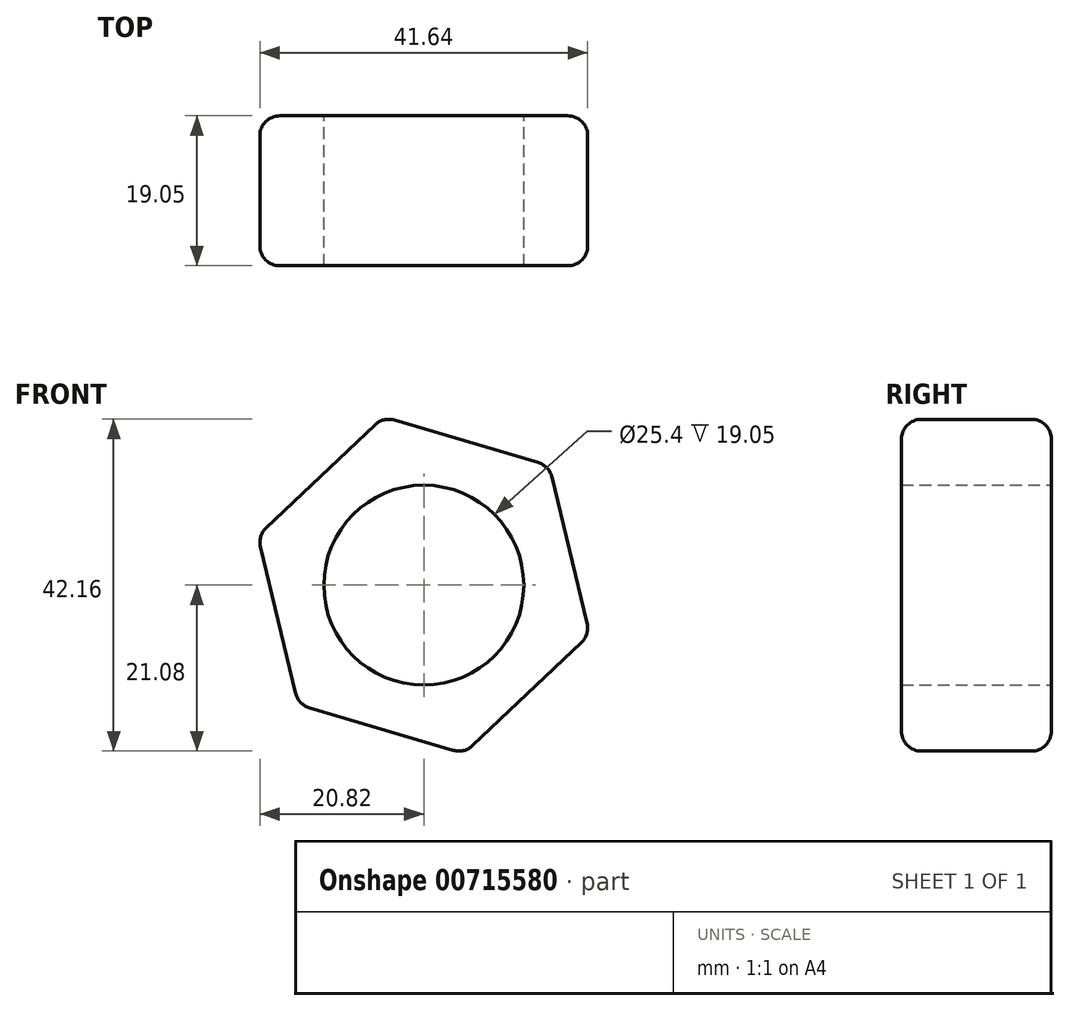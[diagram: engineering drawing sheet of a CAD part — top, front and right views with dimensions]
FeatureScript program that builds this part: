
annotation { "Feature Type Name" : "Feature", "Feature Type Description" : "" }
export const myFeature = defineFeature(function(context is Context, id is Id, definition is map)
    precondition{}
    {
        {
            var Q0;
            Q0=qCreatedBy(makeId("Front.planeOp"),FACE);
            var sketch = newSketch(context, id + "F0", { "sketchPlane" : qUnion([Q0])});
            skCircle(sketch, "E0", {"center": v(0, 0) * mm, "radius": 12.7 * mm});
            skCircle(sketch, "E1.cCircle", {"center": v(0, 0) * mm, "radius": 19.05 * mm, "construction": true});
            skLineSegment(sketch, "E1.0", {"start": v(21.1, -6.24) * mm, "end": v(5.14, -21.39) * mm});
            skLineSegment(sketch, "E1.1", {"start": v(5.14, -21.39) * mm, "end": v(-15.95, -15.15) * mm});
            skLineSegment(sketch, "E1.2", {"start": v(-15.95, -15.15) * mm, "end": v(-21.1, 6.24) * mm});
            skLineSegment(sketch, "E1.3", {"start": v(-21.1, 6.24) * mm, "end": v(-5.14, 21.39) * mm});
            skLineSegment(sketch, "E1.4", {"start": v(-5.14, 21.39) * mm, "end": v(15.95, 15.15) * mm});
            skLineSegment(sketch, "E1.5", {"start": v(15.95, 15.15) * mm, "end": v(21.1, -6.24) * mm});
            skSolve(sketch);
        }
        {
            var Q0;
            Q0 = qSketchRegion(id + "F0", true);
            extrude(context, id + "F1", {"entities" : qUnion([Q0]), "depth" : 19.05 * mm, "offsetDistance" : 25.4 * mm});
        }
        {
            var Q0;
            Q0=makeQuery(id+"F1.opExtrude","CAP_EDGE",EDGE,{"disambiguationData":[OSD([sQuery(id+"F0.wireOp",EDGE,"E1.1")])],"isStart":false});
            var Q1;
            Q1=makeQuery(id+"F1.opExtrude","CAP_EDGE",EDGE,{"disambiguationData":[OSD([sQuery(id+"F0.wireOp",EDGE,"E1.0")])],"isStart":false});
            var Q2;
            Q2=makeQuery(id+"F1.opExtrude","CAP_EDGE",EDGE,{"disambiguationData":[OSD([sQuery(id+"F0.wireOp",EDGE,"E1.5")])],"isStart":false});
            var Q3;
            Q3=makeQuery(id+"F1.opExtrude","CAP_EDGE",EDGE,{"disambiguationData":[OSD([sQuery(id+"F0.wireOp",EDGE,"E1.4")])],"isStart":false});
            var Q4;
            Q4=makeQuery(id+"F1.opExtrude","CAP_EDGE",EDGE,{"disambiguationData":[OSD([sQuery(id+"F0.wireOp",EDGE,"E1.3")])],"isStart":false});
            var Q5;
            Q5=makeQuery(id+"F1.opExtrude","CAP_EDGE",EDGE,{"disambiguationData":[OSD([sQuery(id+"F0.wireOp",EDGE,"E1.2")])],"isStart":false});
            var Q6;
            Q6=makeQuery(id+"F1.opExtrude","CAP_EDGE",EDGE,{"disambiguationData":[OSD([sQuery(id+"F0.wireOp",EDGE,"E1.1")])],"isStart":true});
            var Q7;
            Q7=makeQuery(id+"F1.opExtrude","SWEPT_EDGE",EDGE,{"disambiguationData":[OSD([sQuery(id+"F0.wireOp",EDGE,"E1.1"),sQuery(id+"F0.wireOp",EDGE,"E1.2")])]});
            var Q8;
            Q8=makeQuery(id+"F1.opExtrude","CAP_EDGE",EDGE,{"disambiguationData":[OSD([sQuery(id+"F0.wireOp",EDGE,"E1.2")])],"isStart":true});
            var Q9;
            Q9=makeQuery(id+"F1.opExtrude","CAP_EDGE",EDGE,{"disambiguationData":[OSD([sQuery(id+"F0.wireOp",EDGE,"E1.3")])],"isStart":true});
            var Q10;
            Q10=makeQuery(id+"F1.opExtrude","CAP_EDGE",EDGE,{"disambiguationData":[OSD([sQuery(id+"F0.wireOp",EDGE,"E1.4")])],"isStart":true});
            var Q11;
            Q11=makeQuery(id+"F1.opExtrude","CAP_EDGE",EDGE,{"disambiguationData":[OSD([sQuery(id+"F0.wireOp",EDGE,"E1.5")])],"isStart":true});
            var Q12;
            Q12=makeQuery(id+"F1.opExtrude","CAP_EDGE",EDGE,{"disambiguationData":[OSD([sQuery(id+"F0.wireOp",EDGE,"E1.0")])],"isStart":true});
            var Q13;
            Q13=makeQuery(id+"F1.opExtrude","SWEPT_EDGE",EDGE,{"disambiguationData":[OSD([sQuery(id+"F0.wireOp",EDGE,"E1.2"),sQuery(id+"F0.wireOp",EDGE,"E1.3")])]});
            var Q14;
            Q14=makeQuery(id+"F1.opExtrude","SWEPT_EDGE",EDGE,{"disambiguationData":[OSD([sQuery(id+"F0.wireOp",EDGE,"E1.3"),sQuery(id+"F0.wireOp",EDGE,"E1.4")])]});
            var Q15;
            Q15=makeQuery(id+"F1.opExtrude","SWEPT_EDGE",EDGE,{"disambiguationData":[OSD([sQuery(id+"F0.wireOp",EDGE,"E1.4"),sQuery(id+"F0.wireOp",EDGE,"E1.5")])]});
            var Q16;
            Q16=makeQuery(id+"F1.opExtrude","SWEPT_EDGE",EDGE,{"disambiguationData":[OSD([sQuery(id+"F0.wireOp",EDGE,"E1.0"),sQuery(id+"F0.wireOp",EDGE,"E1.5")])]});
            var Q17;
            Q17=makeQuery(id+"F1.opExtrude","SWEPT_EDGE",EDGE,{"disambiguationData":[OSD([sQuery(id+"F0.wireOp",EDGE,"E1.0"),sQuery(id+"F0.wireOp",EDGE,"E1.1")])]});
            fillet(context, id + "F2", {"entities" : qUnion([Q0, Q1, Q2, Q3, Q4, Q5, Q6, Q7, Q8, Q9, Q10, Q11, Q12, Q13, Q14, Q15, Q16, Q17]), "radius" : 2.54 * mm, "tangentPropagation" : true, "allowEdgeOverflow" : false});
        }
    });
